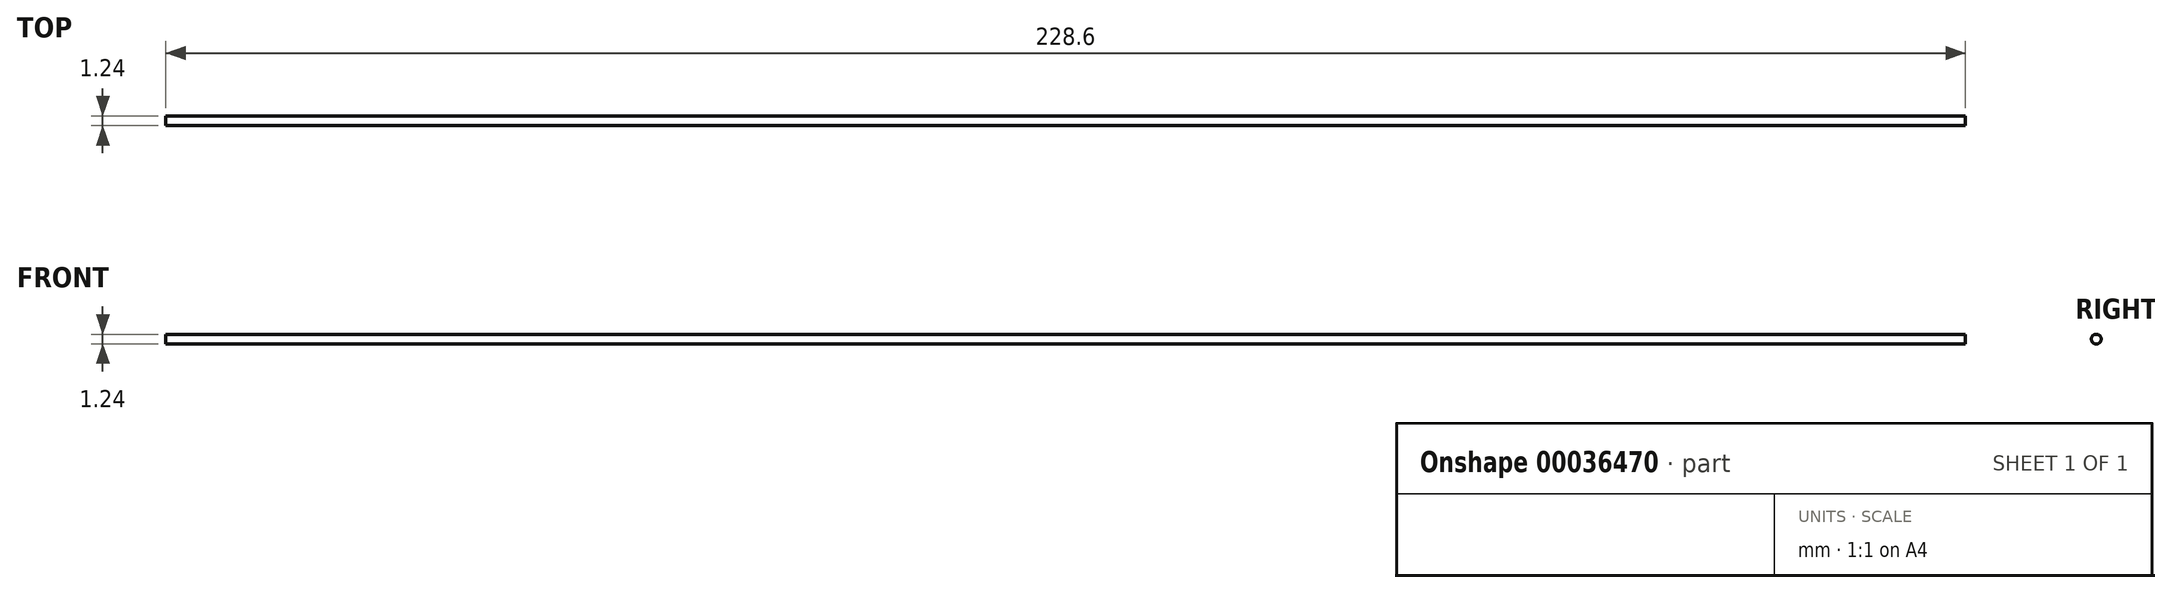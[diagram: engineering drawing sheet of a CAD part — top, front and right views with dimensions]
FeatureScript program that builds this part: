
annotation { "Feature Type Name" : "Feature", "Feature Type Description" : "" }
export const myFeature = defineFeature(function(context is Context, id is Id, definition is map)
    precondition{}
    {
        {
            var Q0;
            Q0=qCreatedBy(makeId("Right.planeOp"),FACE);
            var sketch = newSketch(context, id + "F0", { "sketchPlane" : qUnion([Q0])});
            skCircle(sketch, "E0", {"center": v(0, 0) * mm, "radius": 0.62 * mm});
            skSolve(sketch);
        }
        {
            var Q0;
            Q0 = qSketchRegion(id + "F0", true);
            extrude(context, id + "F1", {"entities" : qUnion([Q0]), "oppositeDirection" : true, "depth" : 228.6 * mm});
        }
        {
            var Q0;
            Q0=makeQuery(id+"F1.opExtrude","SWEPT_BODY",BODY,{"disambiguationData":[OSD([sQuery(id+"F0.wireOp",EDGE,"E0")])]});
            transform(context, id + "F2", {"entities" : qUnion([Q0]), "transformType" : TransformType.TRANSLATION_3D, "dx" : 0 * mm, "dy" : 0 * mm, "dz" : 0 * mm, "makeCopy" : true});
        }
        {
            var Q0;
            Q0=makeQuery(id+"F1.opExtrude","SWEPT_BODY",BODY,{"disambiguationData":[OSD([sQuery(id+"F0.wireOp",EDGE,"E0")])]});
            transform(context, id + "F3", {"entities" : qUnion([Q0]), "transformType" : TransformType.TRANSLATION_3D, "dx" : 0 * mm, "dy" : 0 * mm, "dz" : 0 * mm, "makeCopy" : true});
        }
        {
            var Q0;
            Q0=makeQuery(id+"F2.opPattern","COPY",BODY,{"derivedFrom":makeQuery(id+"F1.opExtrude","SWEPT_BODY",BODY,{"disambiguationData":[OSD([sQuery(id+"F0.wireOp",EDGE,"E0")])]}),"instanceName":"1"});
            deleteBodies(context, id + "F4", {"entities" : qUnion([Q0])});
        }
        {
            var Q0;
            Q0=makeQuery(id+"F3.opPattern","COPY",BODY,{"derivedFrom":makeQuery(id+"F1.opExtrude","SWEPT_BODY",BODY,{"disambiguationData":[OSD([sQuery(id+"F0.wireOp",EDGE,"E0")])]}),"instanceName":"1"});
            deleteBodies(context, id + "F5", {"entities" : qUnion([Q0])});
        }
    });
